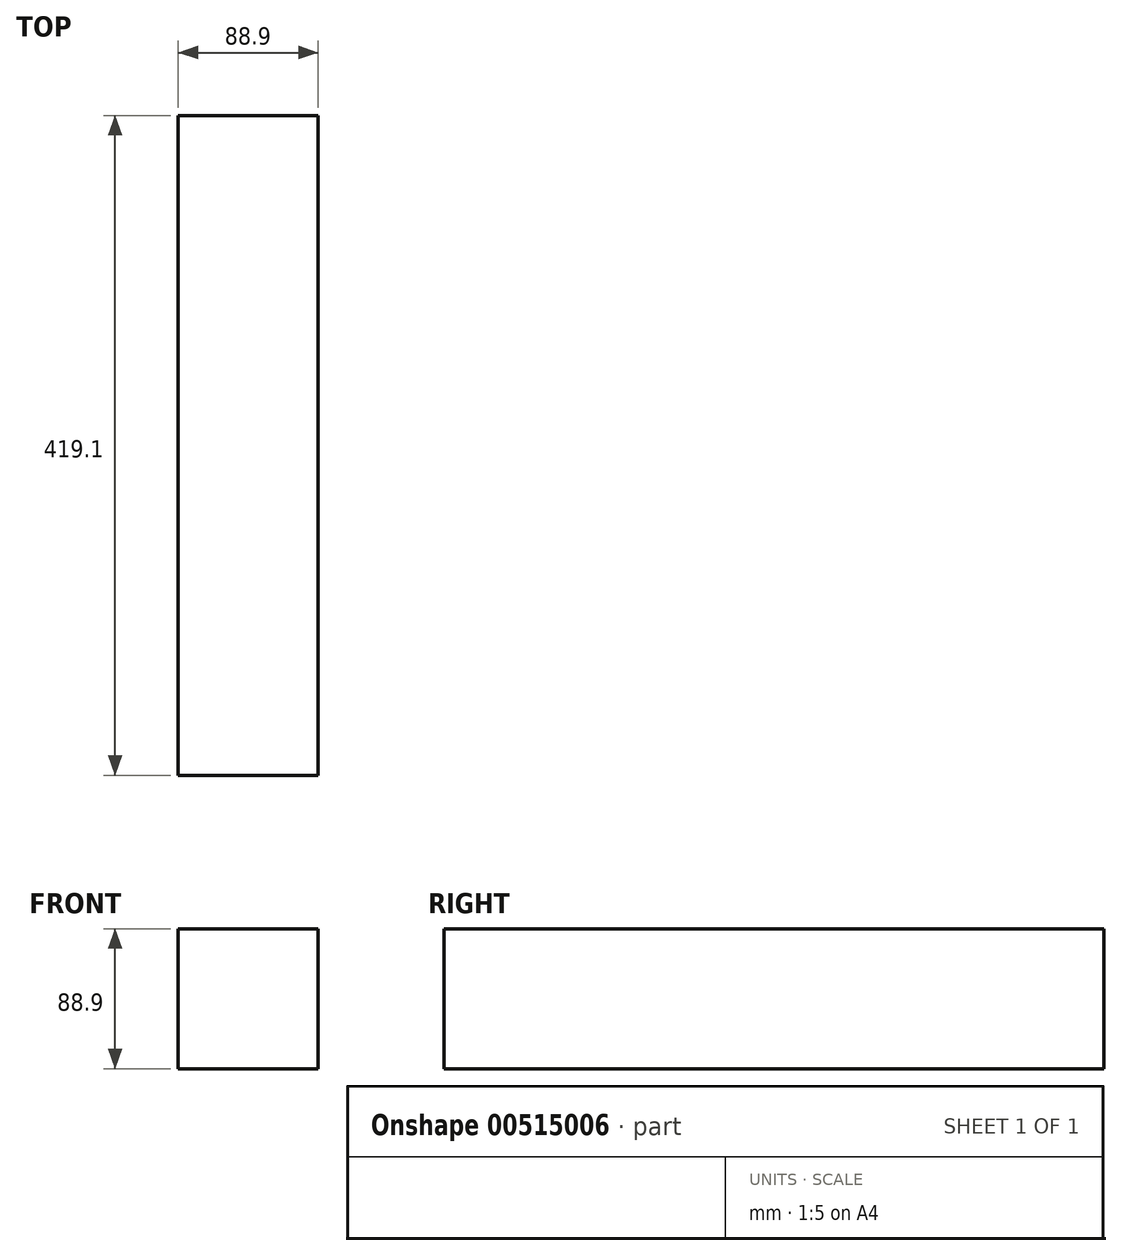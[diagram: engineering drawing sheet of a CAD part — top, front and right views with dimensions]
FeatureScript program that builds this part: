
annotation { "Feature Type Name" : "Feature", "Feature Type Description" : "" }
export const myFeature = defineFeature(function(context is Context, id is Id, definition is map)
    precondition{}
    {
        {
            var Q0;
            Q0=qCreatedBy(makeId("Top.planeOp"),FACE);
            var sketch = newSketch(context, id + "F0", { "sketchPlane" : qUnion([Q0])});
            skLineSegment(sketch, "E0.bottom", {"start": v(0, -0.34) * mm, "end": v(88.9, -0.34) * mm});
            skLineSegment(sketch, "E0.top", {"start": v(0, 418.76) * mm, "end": v(88.9, 418.76) * mm});
            skLineSegment(sketch, "E0.left", {"start": v(0, -0.34) * mm, "end": v(0, 418.76) * mm});
            skLineSegment(sketch, "E0.right", {"start": v(88.9, -0.34) * mm, "end": v(88.9, 418.76) * mm});
            skSolve(sketch);
        }
        {
            var Q0;
            Q0=makeQuery(id+"F0.imprint","IMPRINT",FACE,{"disambiguationData":[TD([[makeQuery(id+"F0.imprint","IMPRINT",EDGE,{"derivedFrom":sQuery(id+"F0.wireOp",EDGE,"E0.bottom")}),1.0]])]});
            extrude(context, id + "F1", {"entities" : qUnion([Q0]), "depth" : 88.9 * mm, "offsetDistance" : 25.4 * mm});
        }
    });
